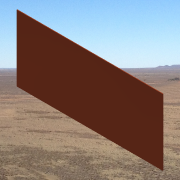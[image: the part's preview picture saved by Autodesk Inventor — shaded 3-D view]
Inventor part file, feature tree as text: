
AUTODESK INVENTOR PART (.ipt)
format: ipt  version: 2014 SP1 (Build 180222100, 222)  size: 109,568 bytes
history: native  units: in
note: dims shown in document units (in); Inventor stores cm internally (conversion verified against a paired STEP export)
features: extrude x1, sketch x1
ambient origin geometry x8: Origin, YZ Plane, XZ Plane, XY Plane, X Axis, Y Axis, Z Axis, Center Point
bodies: Solid1 (feature_tree)
feature tree (2):
  extrude  "Extrusion1"  Depth=10.0in
  sketch  "Sketch1"  dims[d0=22.0in d1=10.0in d2=0.1in d3=0.0in]
